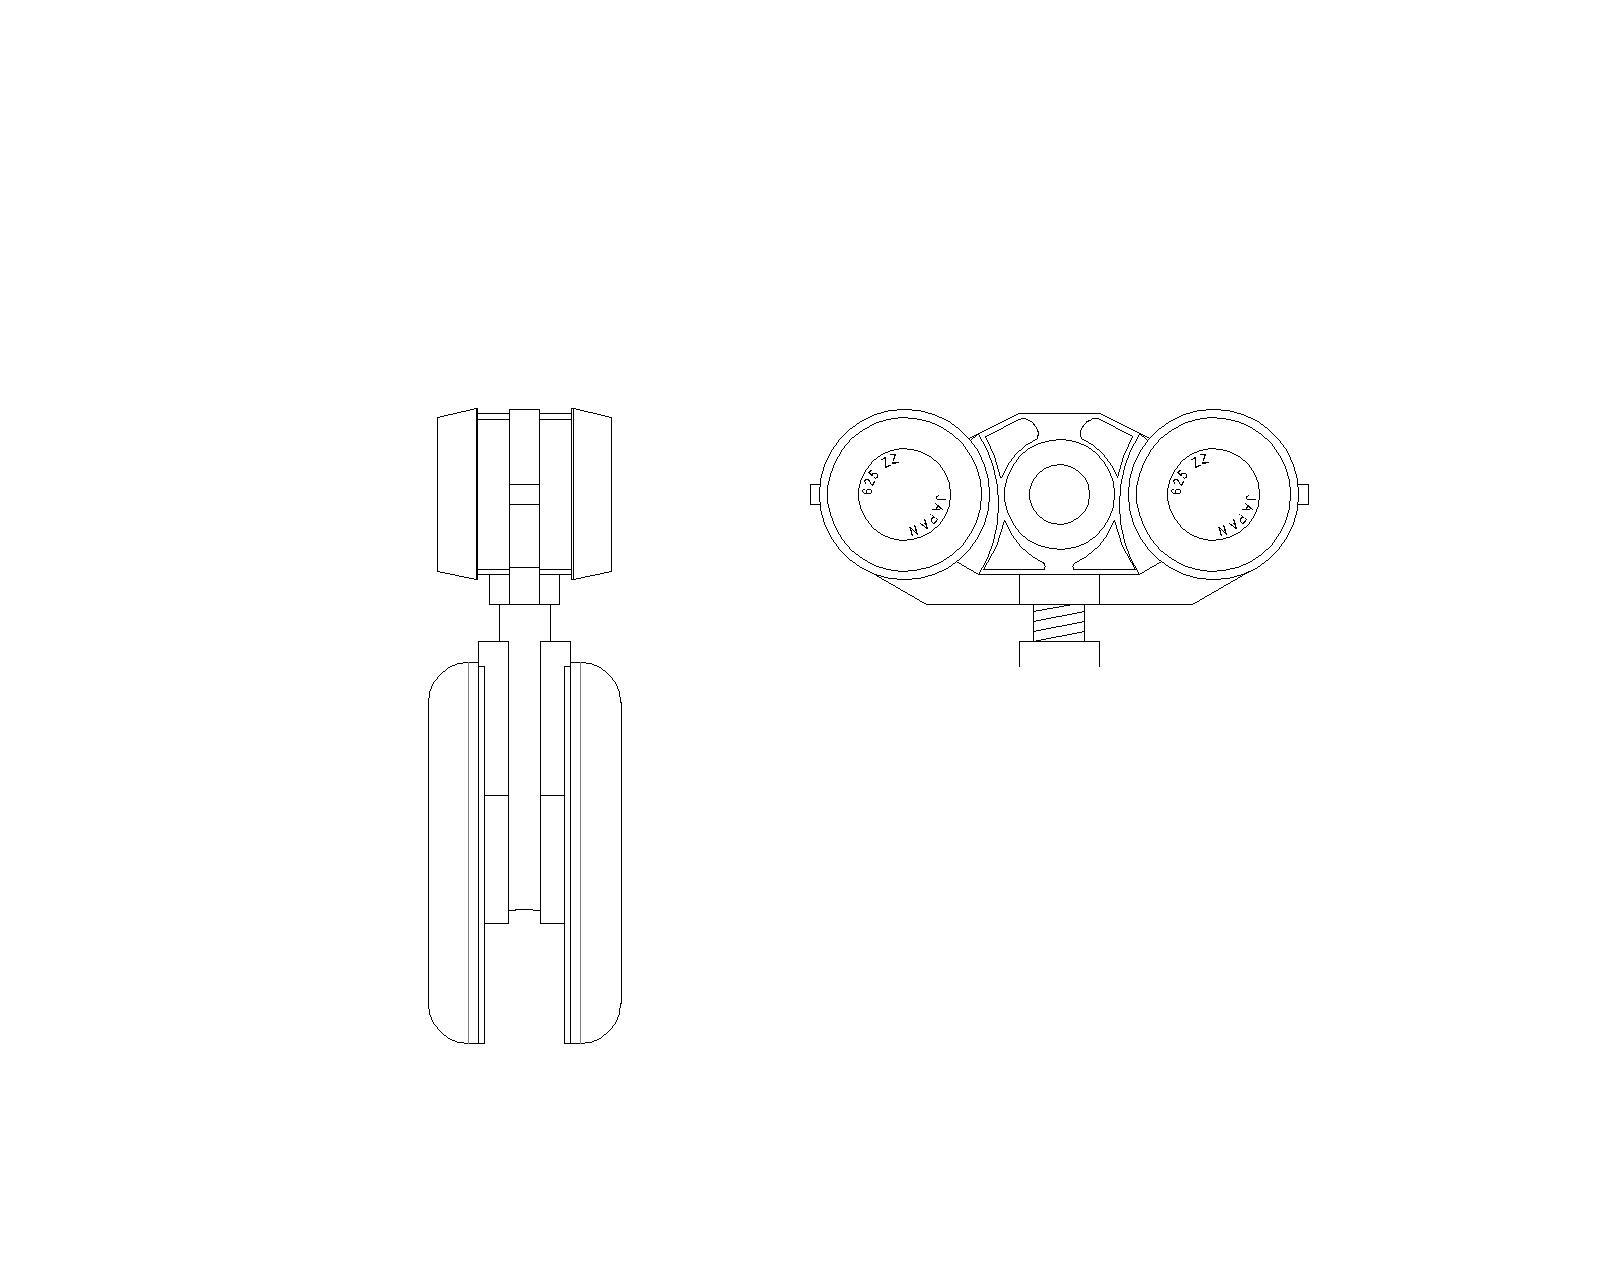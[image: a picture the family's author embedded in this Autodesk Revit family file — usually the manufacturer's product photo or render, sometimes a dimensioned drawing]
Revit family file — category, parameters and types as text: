
# Revit family: PRL_Ruby_Series
name_source: partatom
category: Doors
units: mm (PartAtom-declared; Revit-internal decimal feet)

## family parameters
Always vertical = Yes
Classification Number = 23.30.10.00
Cut with Voids When Loaded = No
Host = Wall
Room Calculation Point = No
Shared = No

## types (1)
- PRL_Ruby_Series
    A_X = 0
    Analytic Construction = <Ninguno>
    DWM = 1' - 6"
    Define Thermal Properties by = Schematic Type
    Frame Projection Ext. = 0' - 1"
    Frame Projection Int. = 0' - 1"
    Frame Width = 0' - 3"
    Function = Interior
    Height = 7' - 0"
    T_H = 11' - 0"
    W_OXXO_I = 7' - 0 1/2"
    Wall Closure = By host
    Width = 7' - 0"
    XCFX = 01 Ruby Series : Wall Mount X
    XCFXX = 02 Ruby Series : Wall Mount XX
    XCWOX = 05 Ruby Series : Glass Mount OXXO
    XCWX = 03 Ruby Series : Glass Mount OX
    XCWXX = 04 Ruby Series : Glass Mount OXO
    XG12 = 1/2"
    XG38 = 3/8"
    XR3 = Glass Mount
    XRM = 0

## geometry (parser evidence)
native form markers: Sweep x94
no freeform markers — native parametric forms only
